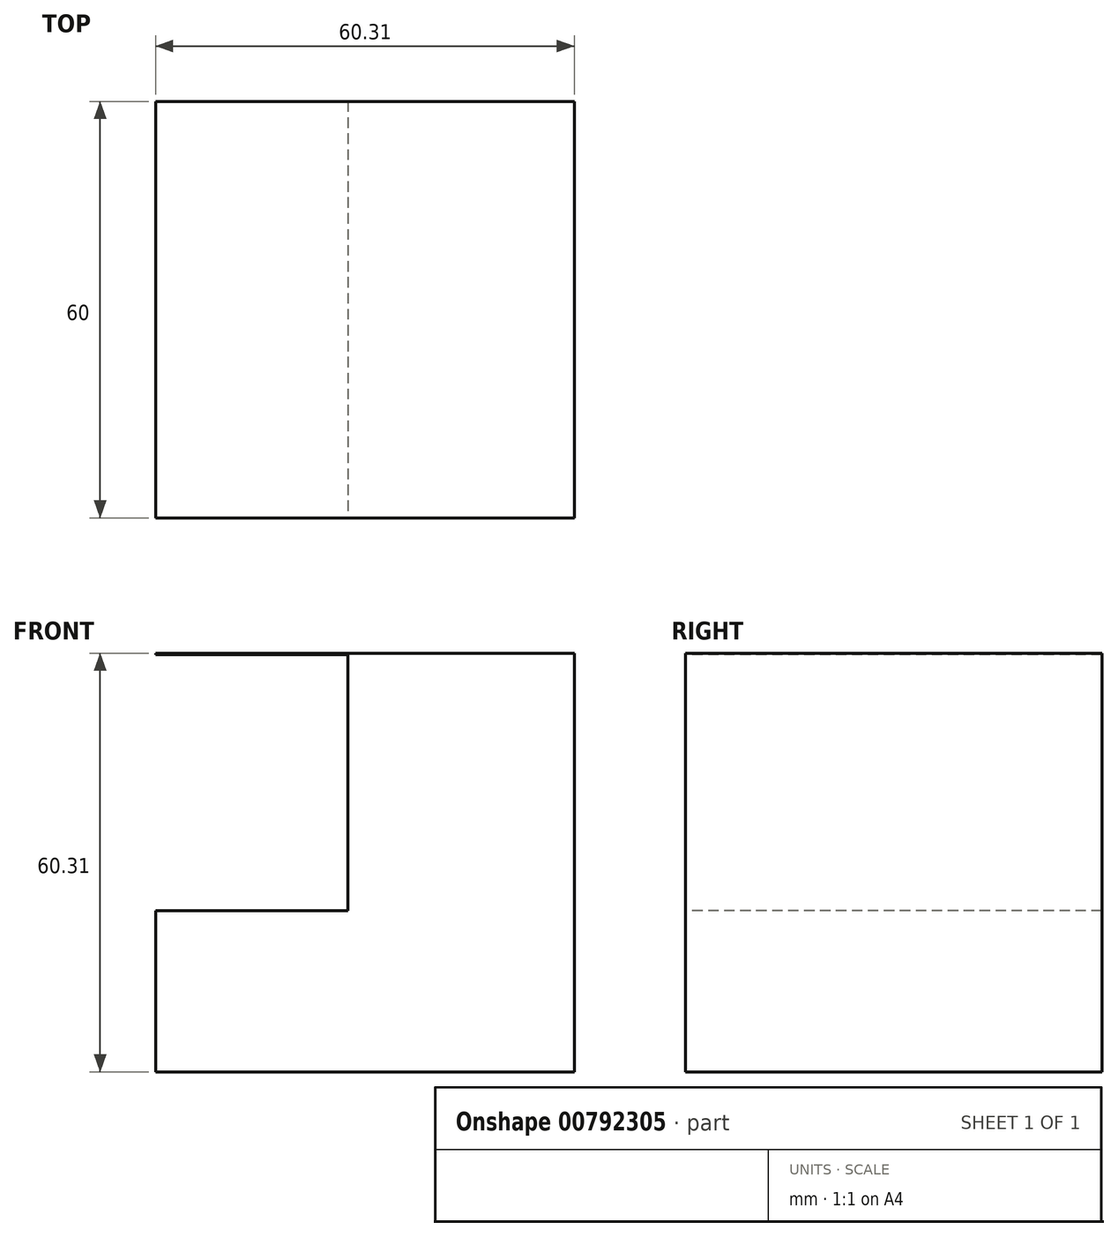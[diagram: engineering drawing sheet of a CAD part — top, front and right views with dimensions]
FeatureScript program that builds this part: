
annotation { "Feature Type Name" : "Feature", "Feature Type Description" : "" }
export const myFeature = defineFeature(function(context is Context, id is Id, definition is map)
    precondition{}
    {
        {
            var Q0;
            Q0=qCreatedBy(makeId("Front.planeOp"),FACE);
            var sketch = newSketch(context, id + "F0", { "sketchPlane" : qUnion([Q0])});
            skLineSegment(sketch, "E0.bottom", {"start": v(39.52, 52.7) * mm, "end": v(-20.79, 52.7) * mm});
            skLineSegment(sketch, "E0.top", {"start": v(39.52, -7.61) * mm, "end": v(-20.79, -7.61) * mm});
            skLineSegment(sketch, "E0.left", {"start": v(39.52, 52.7) * mm, "end": v(39.52, -7.61) * mm});
            skLineSegment(sketch, "E0.right", {"start": v(-20.79, 52.7) * mm, "end": v(-20.79, -7.61) * mm});
            skSolve(sketch);
        }
        {
            var Q0;
            Q0=makeQuery(id+"F0.imprint","IMPRINT",FACE,{"disambiguationData":[TD([[makeQuery(id+"F0.imprint","IMPRINT",EDGE,{"derivedFrom":sQuery(id+"F0.wireOp",EDGE,"E0.bottom")}),1.0]])]});
            extrude(context, id + "F1", {"entities" : qUnion([Q0]), "endBound" : BoundingType.SYMMETRIC, "depth" : 60 * mm, "offsetDistance" : 25 * mm});
        }
        {
            var Q0;
            Q0=qCreatedBy(makeId("Front.planeOp"),FACE);
            var sketch = newSketch(context, id + "F2", { "sketchPlane" : qUnion([Q0])});
            skLineSegment(sketch, "E1.bottom", {"start": v(6.93, 52.5) * mm, "end": v(-20.79, 52.5) * mm});
            skLineSegment(sketch, "E1.top", {"start": v(6.93, 15.61) * mm, "end": v(-20.79, 15.61) * mm});
            skLineSegment(sketch, "E1.left", {"start": v(6.93, 52.5) * mm, "end": v(6.93, 15.61) * mm});
            skLineSegment(sketch, "E1.right", {"start": v(-20.79, 52.5) * mm, "end": v(-20.79, 15.61) * mm});
            skSolve(sketch);
        }
        {
            var Q0;
            Q0 = qSketchRegion(id + "F2", true);
            extrude(context, id + "F3", {"entities" : qUnion([Q0]), "operationType" : NewBodyOperationType.REMOVE, "endBound" : BoundingType.SYMMETRIC, "oppositeDirection" : true, "depth" : 161.2 * mm, "offsetDistance" : 25 * mm});
        }
    });
